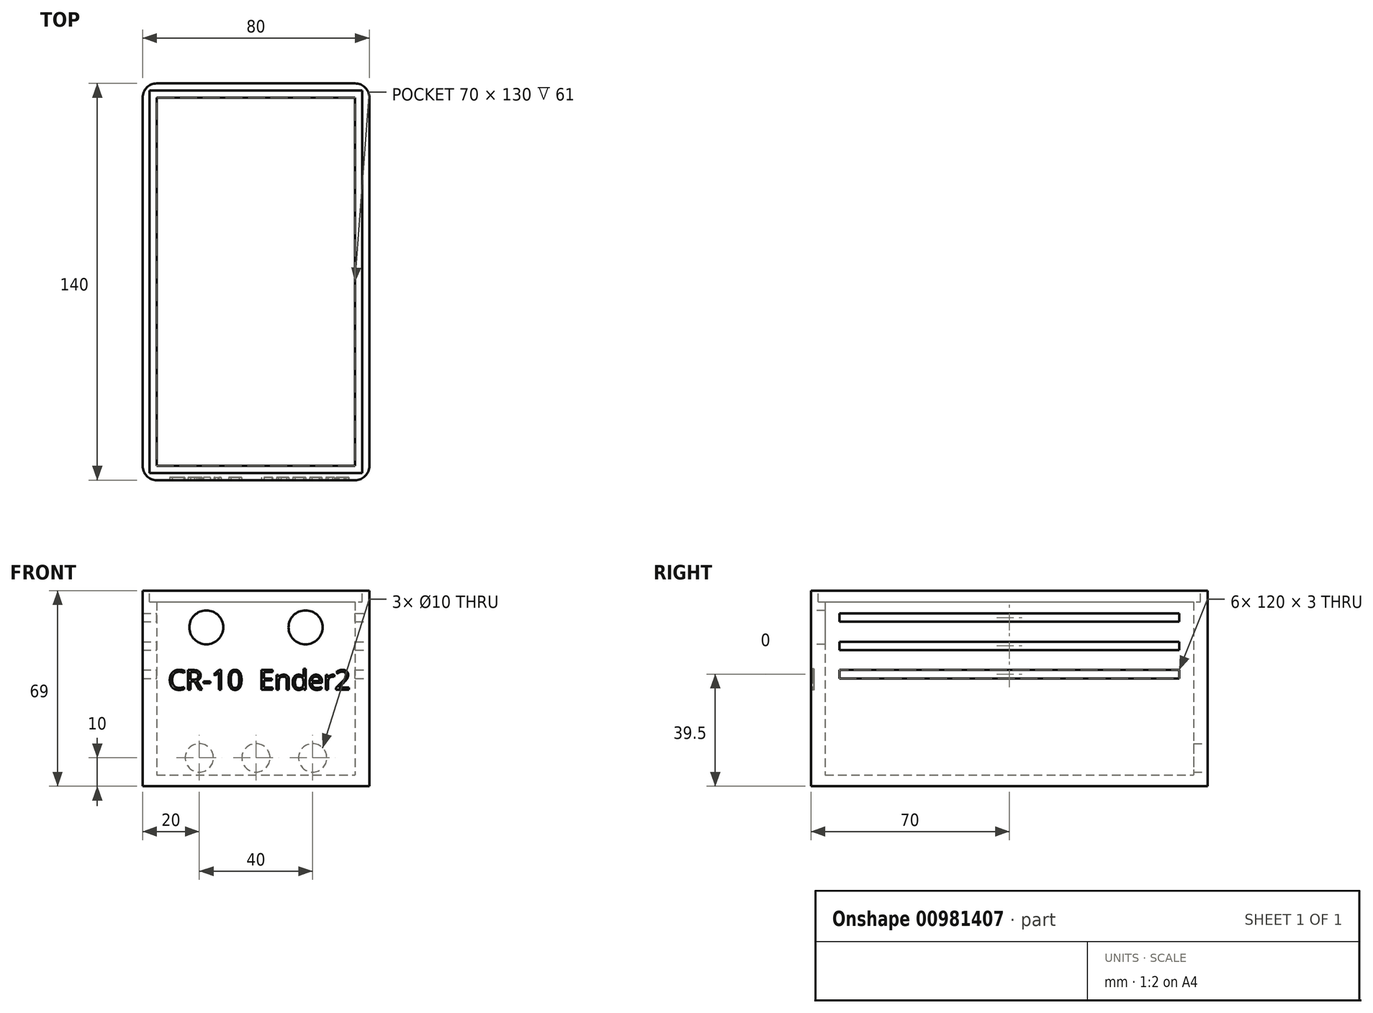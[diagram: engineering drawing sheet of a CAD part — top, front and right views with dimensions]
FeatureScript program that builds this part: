
annotation { "Feature Type Name" : "Feature", "Feature Type Description" : "" }
export const myFeature = defineFeature(function(context is Context, id is Id, definition is map)
    precondition{}
    {
        {
            var Q0;
            Q0=qCreatedBy(makeId("Top.planeOp"),FACE);
            var sketch = newSketch(context, id + "F0", { "sketchPlane" : qUnion([Q0])});
            skLineSegment(sketch, "E0.bottom", {"start": v(-40, -70) * mm, "end": v(40, -70) * mm});
            skLineSegment(sketch, "E0.top", {"start": v(-40, 70) * mm, "end": v(40, 70) * mm});
            skLineSegment(sketch, "E0.left", {"start": v(-40, -70) * mm, "end": v(-40, 70) * mm});
            skLineSegment(sketch, "E0.right", {"start": v(40, -70) * mm, "end": v(40, 70) * mm});
            skPoint(sketch, "E0.middle", {"position": v(0, 0) * mm});
            skSolve(sketch);
        }
        {
            var Q0;
            Q0=makeQuery(id+"F0.imprint","IMPRINT",FACE,{"disambiguationData":[TD([[makeQuery(id+"F0.imprint","IMPRINT",EDGE,{"derivedFrom":sQuery(id+"F0.wireOp",EDGE,"E0.bottom")}),1.0]])]});
            extrude(context, id + "F1", {"entities" : qUnion([Q0]), "depth" : 4 * mm, "offsetDistance" : 25 * mm});
        }
        {
            var Q0;
            Q0=makeQuery(id+"F1.opExtrude","CAP_FACE",FACE,{"disambiguationData":[OSD([sQuery(id+"F0.wireOp",EDGE,"E0.bottom"),sQuery(id+"F0.wireOp",EDGE,"E0.top"),sQuery(id+"F0.wireOp",EDGE,"E0.left"),sQuery(id+"F0.wireOp",EDGE,"E0.right")])],"isStart":false});
            var sketch = newSketch(context, id + "F2", { "sketchPlane" : qUnion([Q0])});
            skLineSegment(sketch, "E1.bottom", {"start": v(-40, -70) * mm, "end": v(40, -70) * mm});
            skLineSegment(sketch, "E1.top", {"start": v(-40, 70) * mm, "end": v(40, 70) * mm});
            skLineSegment(sketch, "E1.left", {"start": v(-40, -70) * mm, "end": v(-40, 70) * mm});
            skLineSegment(sketch, "E1.right", {"start": v(40, -70) * mm, "end": v(40, 70) * mm});
            skPoint(sketch, "E1.middle", {"position": v(0, 0) * mm});
            skLineSegment(sketch, "E2.bottom", {"start": v(-35, -65) * mm, "end": v(35, -65) * mm});
            skLineSegment(sketch, "E2.top", {"start": v(-35, 65) * mm, "end": v(35, 65) * mm});
            skLineSegment(sketch, "E2.left", {"start": v(-35, -65) * mm, "end": v(-35, 65) * mm});
            skLineSegment(sketch, "E2.right", {"start": v(35, -65) * mm, "end": v(35, 65) * mm});
            skSolve(sketch);
        }
        {
            var Q0;
            Q0=makeQuery(id+"F2.imprint","IMPRINT",FACE,{"disambiguationData":[TD([[makeQuery(id+"F2.imprint","IMPRINT",EDGE,{"derivedFrom":sQuery(id+"F2.wireOp",EDGE,"E1.bottom")}),1.0]])]});
            extrude(context, id + "F3", {"entities" : qUnion([Q0]), "operationType" : NewBodyOperationType.ADD, "depth" : 65 * mm, "offsetDistance" : 25 * mm});
        }
        {
            var Q0;
            Q0=makeQuery(id+"F3.boolean.opBoolean","MERGE",FACE,{"derivedFrom":[makeQuery(id+"F1.opExtrude","SWEPT_FACE",FACE,{"disambiguationData":[OSD([sQuery(id+"F0.wireOp",EDGE,"E0.top")])]}),makeQuery(id+"F3.opExtrude","SWEPT_FACE",FACE,{"disambiguationData":[OSD([sQuery(id+"F2.wireOp",EDGE,"E1.top")])]})]});
            var sketch = newSketch(context, id + "F4", { "sketchPlane" : qUnion([Q0])});
            skLineSegment(sketch, "E3", {"start": v(-40, 10) * mm, "end": v(40, 10) * mm, "construction": true});
            skCircle(sketch, "E4", {"center": v(0, 10) * mm, "radius": 5 * mm});
            skCircle(sketch, "E5", {"center": v(-20, 10) * mm, "radius": 5 * mm});
            skCircle(sketch, "E6", {"center": v(20, 10) * mm, "radius": 5 * mm});
            skSolve(sketch);
        }
        {
            var Q0;
            Q0=makeQuery(id+"F4.imprint","IMPRINT",FACE,{"disambiguationData":[TD([[makeQuery(id+"F4.imprint","IMPRINT",EDGE,{"derivedFrom":sQuery(id+"F4.wireOp",EDGE,"E5")}),1.0]])]});
            var Q1;
            Q1=makeQuery(id+"F4.imprint","IMPRINT",FACE,{"disambiguationData":[TD([[makeQuery(id+"F4.imprint","IMPRINT",EDGE,{"derivedFrom":sQuery(id+"F4.wireOp",EDGE,"E4")}),1.0]])]});
            var Q2;
            Q2=makeQuery(id+"F4.imprint","IMPRINT",FACE,{"disambiguationData":[TD([[makeQuery(id+"F4.imprint","IMPRINT",EDGE,{"derivedFrom":sQuery(id+"F4.wireOp",EDGE,"E6")}),1.0]])]});
            extrude(context, id + "F5", {"entities" : qUnion([Q0, Q1, Q2]), "operationType" : NewBodyOperationType.REMOVE, "oppositeDirection" : true, "depth" : 25 * mm, "offsetDistance" : 25 * mm});
        }
        {
            var Q0;
            Q0=makeQuery(id+"F3.boolean.opBoolean","MERGE",FACE,{"derivedFrom":[makeQuery(id+"F1.opExtrude","SWEPT_FACE",FACE,{"disambiguationData":[OSD([sQuery(id+"F0.wireOp",EDGE,"E0.right")])]}),makeQuery(id+"F3.opExtrude","SWEPT_FACE",FACE,{"disambiguationData":[OSD([sQuery(id+"F2.wireOp",EDGE,"E1.right")])]})]});
            var sketch = newSketch(context, id + "F6", { "sketchPlane" : qUnion([Q0])});
            skLineSegment(sketch, "E7.bottom", {"start": v(-60, 61) * mm, "end": v(60, 61) * mm});
            skLineSegment(sketch, "E7.top", {"start": v(-60, 58) * mm, "end": v(60, 58) * mm});
            skLineSegment(sketch, "E7.left", {"start": v(-60, 61) * mm, "end": v(-60, 58) * mm});
            skLineSegment(sketch, "E7.right", {"start": v(60, 61) * mm, "end": v(60, 58) * mm});
            skLineSegment(sketch, "E8.0.1.0", {"start": v(-60, 48) * mm, "end": v(60, 48) * mm});
            skLineSegment(sketch, "E8.0.1.1", {"start": v(-60, 51) * mm, "end": v(60, 51) * mm});
            skLineSegment(sketch, "E8.0.1.2", {"start": v(60, 51) * mm, "end": v(60, 48) * mm});
            skLineSegment(sketch, "E8.0.1.3", {"start": v(-60, 51) * mm, "end": v(-60, 48) * mm});
            skLineSegment(sketch, "E8.0.2.0", {"start": v(-60, 38) * mm, "end": v(60, 38) * mm});
            skLineSegment(sketch, "E8.0.2.1", {"start": v(-60, 41) * mm, "end": v(60, 41) * mm});
            skLineSegment(sketch, "E8.0.2.2", {"start": v(60, 41) * mm, "end": v(60, 38) * mm});
            skLineSegment(sketch, "E8.0.2.3", {"start": v(-60, 41) * mm, "end": v(-60, 38) * mm});
            skLineSegment(sketch, "E8.direction1", {"start": v(-60, 58) * mm, "end": v(-35, 58) * mm, "construction": true});
            skLineSegment(sketch, "E8.direction2", {"start": v(-60, 58) * mm, "end": v(-60, 48) * mm, "construction": true});
            skSolve(sketch);
        }
        {
            var Q0;
            Q0=makeQuery(id+"F6.imprint","IMPRINT",FACE,{"disambiguationData":[TD([[makeQuery(id+"F6.imprint","IMPRINT",EDGE,{"derivedFrom":sQuery(id+"F6.wireOp",EDGE,"E7.bottom")}),-1.0]])]});
            var Q1;
            Q1=makeQuery(id+"F6.imprint","IMPRINT",FACE,{"disambiguationData":[TD([[makeQuery(id+"F6.imprint","IMPRINT",EDGE,{"derivedFrom":sQuery(id+"F6.wireOp",EDGE,"E8.0.1.0")}),1.0]])]});
            var Q2;
            Q2=makeQuery(id+"F6.imprint","IMPRINT",FACE,{"disambiguationData":[TD([[makeQuery(id+"F6.imprint","IMPRINT",EDGE,{"derivedFrom":sQuery(id+"F6.wireOp",EDGE,"E8.0.2.0")}),1.0]])]});
            extrude(context, id + "F7", {"entities" : qUnion([Q0, Q1, Q2]), "operationType" : NewBodyOperationType.REMOVE, "oppositeDirection" : true, "depth" : 100 * mm, "offsetDistance" : 25 * mm});
        }
        {
            var Q0;
            Q0=makeQuery(id+"F3.boolean.opBoolean","MERGE",EDGE,{"derivedFrom":[makeQuery(id+"F1.opExtrude","SWEPT_EDGE",EDGE,{"disambiguationData":[OSD([sQuery(id+"F0.wireOp",EDGE,"E0.bottom"),sQuery(id+"F0.wireOp",EDGE,"E0.left")])]}),makeQuery(id+"F3.opExtrude","SWEPT_EDGE",EDGE,{"disambiguationData":[OSD([sQuery(id+"F2.wireOp",EDGE,"E1.bottom"),sQuery(id+"F2.wireOp",EDGE,"E1.left")])]})]});
            var Q1;
            Q1=makeQuery(id+"F3.boolean.opBoolean","MERGE",EDGE,{"derivedFrom":[makeQuery(id+"F1.opExtrude","SWEPT_EDGE",EDGE,{"disambiguationData":[OSD([sQuery(id+"F0.wireOp",EDGE,"E0.bottom"),sQuery(id+"F0.wireOp",EDGE,"E0.right")])]}),makeQuery(id+"F3.opExtrude","SWEPT_EDGE",EDGE,{"disambiguationData":[OSD([sQuery(id+"F2.wireOp",EDGE,"E1.bottom"),sQuery(id+"F2.wireOp",EDGE,"E1.right")])]})]});
            var Q2;
            Q2=makeQuery(id+"F3.boolean.opBoolean","MERGE",EDGE,{"derivedFrom":[makeQuery(id+"F1.opExtrude","SWEPT_EDGE",EDGE,{"disambiguationData":[OSD([sQuery(id+"F0.wireOp",EDGE,"E0.top"),sQuery(id+"F0.wireOp",EDGE,"E0.left")])]}),makeQuery(id+"F3.opExtrude","SWEPT_EDGE",EDGE,{"disambiguationData":[OSD([sQuery(id+"F2.wireOp",EDGE,"E1.top"),sQuery(id+"F2.wireOp",EDGE,"E1.left")])]})]});
            var Q3;
            Q3=makeQuery(id+"F3.boolean.opBoolean","MERGE",EDGE,{"derivedFrom":[makeQuery(id+"F1.opExtrude","SWEPT_EDGE",EDGE,{"disambiguationData":[OSD([sQuery(id+"F0.wireOp",EDGE,"E0.top"),sQuery(id+"F0.wireOp",EDGE,"E0.right")])]}),makeQuery(id+"F3.opExtrude","SWEPT_EDGE",EDGE,{"disambiguationData":[OSD([sQuery(id+"F2.wireOp",EDGE,"E1.top"),sQuery(id+"F2.wireOp",EDGE,"E1.right")])]})]});
            fillet(context, id + "F8", {"entities" : qUnion([Q0, Q1, Q2, Q3]), "tangentPropagation" : true, "radius" : 5 * mm, "defaultsChanged" : false, "vertexSettings" : [], "allowEdgeOverflow" : false});
        }
        {
            var Q0;
            Q0=makeQuery(id+"F3.opExtrude","CAP_FACE",FACE,{"disambiguationData":[OSD([sQuery(id+"F2.wireOp",EDGE,"E1.bottom"),sQuery(id+"F2.wireOp",EDGE,"E1.top"),sQuery(id+"F2.wireOp",EDGE,"E1.left"),sQuery(id+"F2.wireOp",EDGE,"E1.right"),sQuery(id+"F2.wireOp",EDGE,"E2.bottom"),sQuery(id+"F2.wireOp",EDGE,"E2.top"),sQuery(id+"F2.wireOp",EDGE,"E2.left"),sQuery(id+"F2.wireOp",EDGE,"E2.right")])],"isStart":false});
            var sketch = newSketch(context, id + "F9", { "sketchPlane" : qUnion([Q0])});
            skLineSegment(sketch, "E9.bottom", {"start": v(-35, -65) * mm, "end": v(35, -65) * mm});
            skLineSegment(sketch, "E9.top", {"start": v(-35, 65) * mm, "end": v(35, 65) * mm});
            skLineSegment(sketch, "E9.left", {"start": v(-35, -65) * mm, "end": v(-35, 65) * mm});
            skLineSegment(sketch, "E9.right", {"start": v(35, -65) * mm, "end": v(35, 65) * mm});
            skPoint(sketch, "E9.middle", {"position": v(0, 0) * mm});
            skLineSegment(sketch, "E10.bottom", {"start": v(-37.5, -67.5) * mm, "end": v(37.5, -67.5) * mm});
            skLineSegment(sketch, "E10.top", {"start": v(-37.5, 67.5) * mm, "end": v(37.5, 67.5) * mm});
            skLineSegment(sketch, "E10.left", {"start": v(-37.5, -67.5) * mm, "end": v(-37.5, 67.5) * mm});
            skLineSegment(sketch, "E10.right", {"start": v(37.5, -67.5) * mm, "end": v(37.5, 67.5) * mm});
            skSolve(sketch);
        }
        {
            var Q0;
            Q0=makeQuery(id+"F9.imprint","IMPRINT",FACE,{"disambiguationData":[TD([[makeQuery(id+"F9.imprint","IMPRINT",EDGE,{"derivedFrom":sQuery(id+"F9.wireOp",EDGE,"E9.bottom")}),-1.0]])]});
            extrude(context, id + "F10", {"entities" : qUnion([Q0]), "operationType" : NewBodyOperationType.REMOVE, "oppositeDirection" : true, "depth" : 4 * mm, "offsetDistance" : 25 * mm});
        }
        {
            var Q0;
            Q0=makeQuery(id+"F3.boolean.opBoolean","MERGE",FACE,{"derivedFrom":[makeQuery(id+"F1.opExtrude","SWEPT_FACE",FACE,{"disambiguationData":[OSD([sQuery(id+"F0.wireOp",EDGE,"E0.bottom")])]}),makeQuery(id+"F3.opExtrude","SWEPT_FACE",FACE,{"disambiguationData":[OSD([sQuery(id+"F2.wireOp",EDGE,"E1.bottom")])]})]});
            var sketch = newSketch(context, id + "F11", { "sketchPlane" : qUnion([Q0])});
            skLineSegment(sketch, "E11", {"start": v(-35, 56.05) * mm, "end": v(35, 56.05) * mm, "construction": true});
            skCircle(sketch, "E12", {"center": v(-17.5, 56.05) * mm, "radius": 6 * mm});
            skCircle(sketch, "E13", {"center": v(17.5, 56.05) * mm, "radius": 6 * mm});
            skLineSegment(sketch, "E14", {"start": v(0, 69) * mm, "end": v(0, 38.68) * mm, "construction": true});
            skText(sketch, "E15", { "text": "CR-10\n", "fontName": "OpenSans-Regular.ttf"});
            skText(sketch, "E16", { "text": "Ender2\n", "fontName": "OpenSans-Regular.ttf"});
            const initialGuessF11  = {"E15": [-0.031, 0.03405, 1, 0, 0.007], "E16": [0.00104, 0.03405, 1, 0, 0.007]};
            skSetInitialGuess(sketch, initialGuessF11);
            skSolve(sketch);
        }
        {
            var Q0;
            Q0=makeQuery(id+"F11.imprint","IMPRINT",FACE,{"disambiguationData":[TD([[makeQuery(id+"F11.imprint","IMPRINT",EDGE,{"derivedFrom":sQuery(id+"F11.wireOp",EDGE,"E12")}),1.0]])]});
            var Q1;
            Q1=makeQuery(id+"F11.imprint","IMPRINT",FACE,{"disambiguationData":[TD([[makeQuery(id+"F11.imprint","IMPRINT",EDGE,{"derivedFrom":sQuery(id+"F11.wireOp",EDGE,"E13")}),1.0]])]});
            extrude(context, id + "F12", {"entities" : qUnion([Q0, Q1]), "operationType" : NewBodyOperationType.REMOVE, "oppositeDirection" : true, "depth" : 25 * mm, "offsetDistance" : 25 * mm});
        }
        {
            var Q0;
            Q0 = qSketchRegion(id + "F11", true);
            extrude(context, id + "F13", {"entities" : qUnion([Q0]), "operationType" : NewBodyOperationType.REMOVE, "oppositeDirection" : true, "depth" : 1 * mm, "offsetDistance" : 25 * mm});
        }
    });
